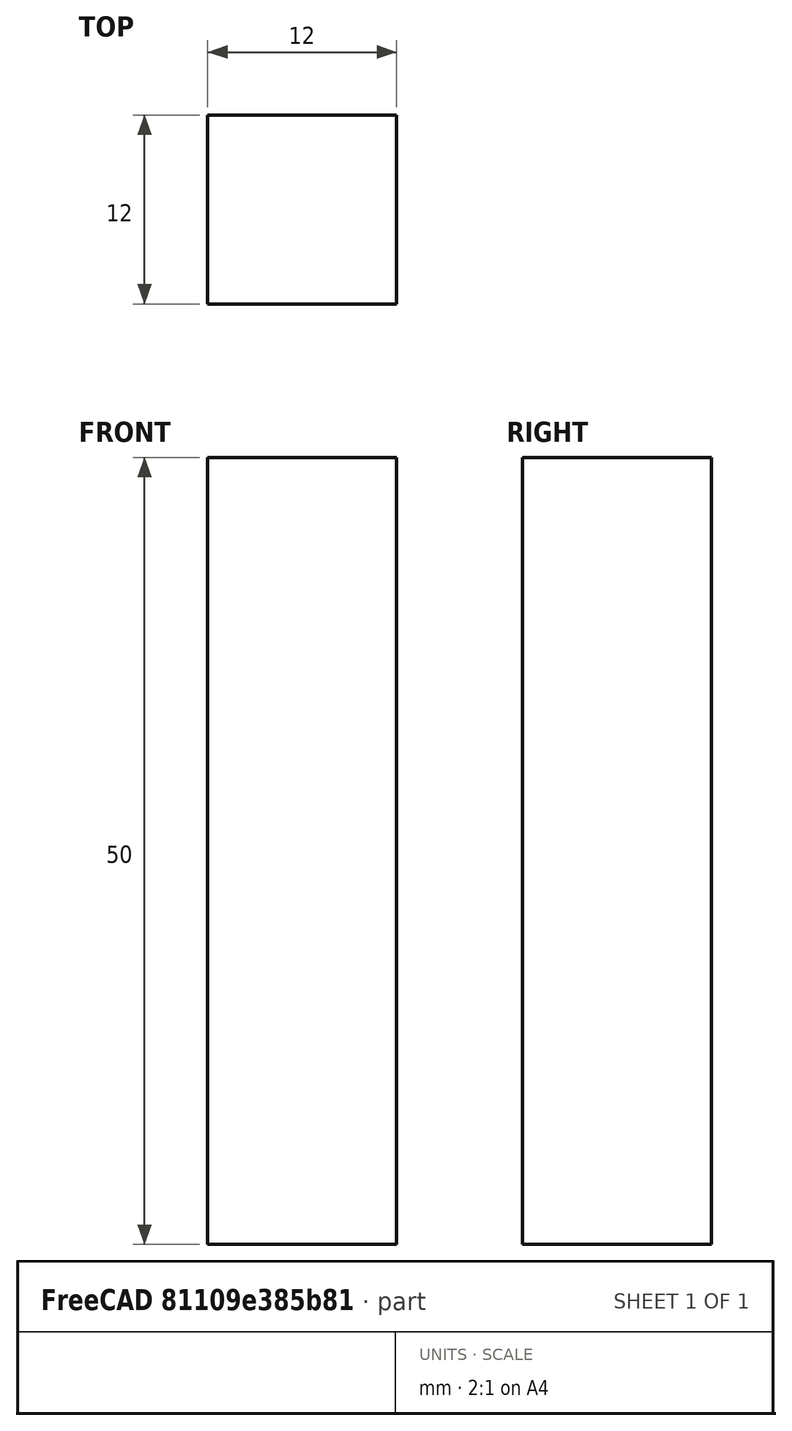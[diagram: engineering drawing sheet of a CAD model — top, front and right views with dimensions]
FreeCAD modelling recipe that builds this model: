
FCSTD DOCUMENT  (FreeCAD 0.15R4671 (Git))
Label: Square Bar 12 EN10059 S235JR
License: All rights reserved
LicenseURL: http://en.wikipedia.org/wiki/All_rights_reserved
objects: Sketcher::SketchObject×1, Part::Extrusion×1
note: 2 computed .brp shape members not serialized (recipe doc carries the construction recipe); baked Part::Feature solids carry a one-line shape summary decoded from their .brp

FEATURE [Sketcher::SketchObject] Sketch
  sketch-geometry (4):
    g0: LineSegment StartX=-6 StartY=-6 StartZ=0 EndX=6 EndY=-6 EndZ=0
    g1: LineSegment StartX=6 StartY=-6 StartZ=0 EndX=6 EndY=6 EndZ=0
    g2: LineSegment StartX=6 StartY=6 StartZ=0 EndX=-6 EndY=6 EndZ=0
    g3: LineSegment StartX=-6 StartY=6 StartZ=0 EndX=-6 EndY=-6 EndZ=0
  constraints (12):
    c: Coincident(g0,g1)
    c: Coincident(g1,g2)
    c: Coincident(g2,g3)
    c: Coincident(g3,g0)
    c: Horizontal(g0)
    c: Horizontal(g2)
    c: Vertical(g1)
    c: Vertical(g3)
    c: Symmetric(g1,g0,g-1)
    c: Symmetric(g2,g1,g-2)
    c: Equal(g1,g2)
    c: DistanceY(g1) = 12
FEATURE [Part::Extrusion] Extrude  label="Square Bar 12 EN10059 S235JR"
  Base = -> Sketch
  Dir = (0,0,50)
  Solid = true
